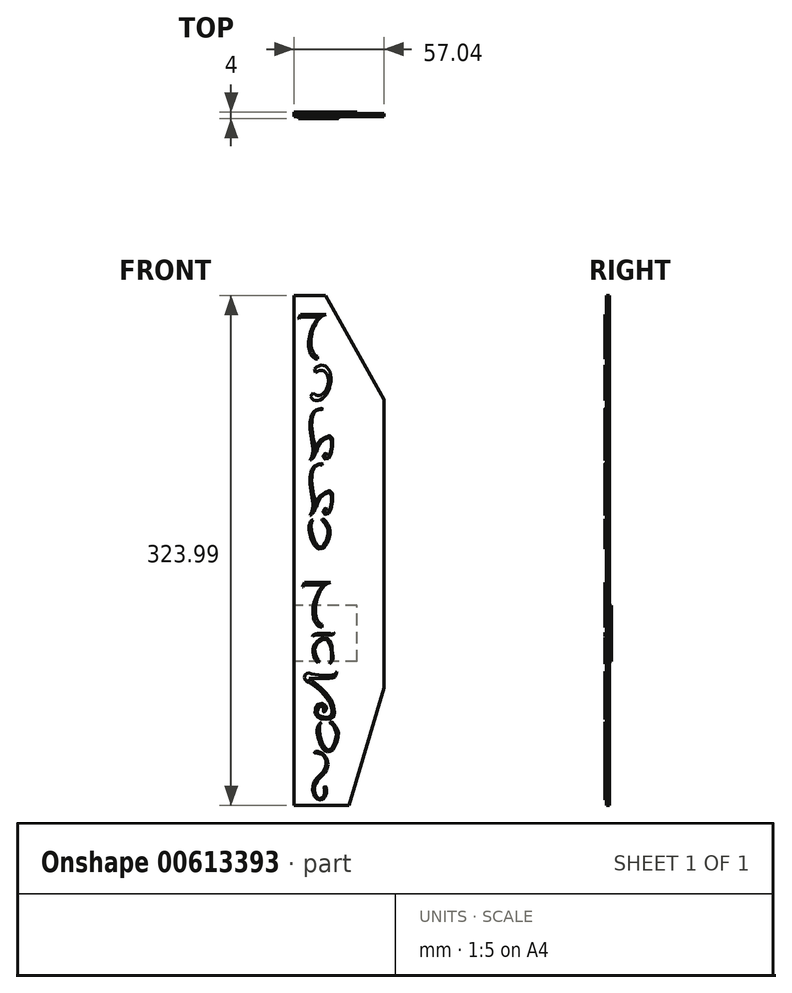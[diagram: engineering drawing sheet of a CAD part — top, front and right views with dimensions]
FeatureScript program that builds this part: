
annotation { "Feature Type Name" : "Feature", "Feature Type Description" : "" }
export const myFeature = defineFeature(function(context is Context, id is Id, definition is map)
    precondition{}
    {
        {
            var Q0;
            Q0=qCreatedBy(makeId("Front.planeOp"),FACE);
            var sketch = newSketch(context, id + "F0", { "sketchPlane" : qUnion([Q0])});
            skLineSegment(sketch, "E0", {"start": v(0, 0) * mm, "end": v(40, 0) * mm});
            skLineSegment(sketch, "E1", {"start": v(40, 0) * mm, "end": v(57.04, 0) * mm});
            skLineSegment(sketch, "E2", {"start": v(57.04, 0) * mm, "end": v(57.04, 166.67) * mm});
            skLineSegment(sketch, "E3", {"start": v(0, 200) * mm, "end": v(0, 0) * mm});
            skLineSegment(sketch, "E4", {"start": v(57.04, 166.67) * mm, "end": v(19.79, 232.6) * mm});
            skPoint(sketch, "E5.center.orphan", {"position": v(28.52, 183.33) * mm});
            skLineSegment(sketch, "E6", {"start": v(19.79, 232.6) * mm, "end": v(0, 232.6) * mm});
            skLineSegment(sketch, "E7", {"start": v(0, 232.6) * mm, "end": v(0, 200) * mm});
            skLineSegment(sketch, "E8", {"start": v(57.04, 0) * mm, "end": v(57.04, -16.7) * mm});
            skLineSegment(sketch, "E9", {"start": v(34.85, -91.4) * mm, "end": v(0, -91.4) * mm});
            skLineSegment(sketch, "E10", {"start": v(0, -91.4) * mm, "end": v(0, 0) * mm});
            skLineSegment(sketch, "E11", {"start": v(34.85, -91.4) * mm, "end": v(57.04, -16.7) * mm});
            skSolve(sketch);
        }
        {
            var Q0;
            Q0=makeQuery(id+"F0.imprint","IMPRINT",FACE,{"disambiguationData":[TD([[makeQuery(id+"F0.imprint","IMPRINT",EDGE,{"derivedFrom":sQuery(id+"F0.wireOp",EDGE,"E0")}),1.0]])]});
            var Q1;
            Q1=makeQuery(id+"F0.imprint","IMPRINT",FACE,{"disambiguationData":[TD([[makeQuery(id+"F0.imprint","IMPRINT",EDGE,{"derivedFrom":sQuery(id+"F0.wireOp",EDGE,"E0")}),-1.0]])]});
            extrude(context, id + "F1", {"entities" : qUnion([Q0, Q1]), "depth" : 2 * mm, "offsetDistance" : 25 * mm});
        }
        {
            var Q0;
            Q0=makeQuery(id+"F1.opExtrude","CAP_FACE",FACE,{"disambiguationData":[OSD([sQuery(id+"F0.wireOp",EDGE,"E0"),sQuery(id+"F0.wireOp",EDGE,"E1"),sQuery(id+"F0.wireOp",EDGE,"E2"),sQuery(id+"F0.wireOp",EDGE,"E3"),sQuery(id+"F0.wireOp",EDGE,"E4"),sQuery(id+"F0.wireOp",EDGE,"E6"),sQuery(id+"F0.wireOp",EDGE,"E7")])],"isStart":true});
            var sketch = newSketch(context, id + "F2", { "sketchPlane" : qUnion([Q0])});
            skLineSegment(sketch, "E12.bottom", {"start": v(-40, 0) * mm, "end": v(0, 0) * mm});
            skLineSegment(sketch, "E12.top", {"start": v(-40, 35.71) * mm, "end": v(0, 35.71) * mm});
            skLineSegment(sketch, "E12.left", {"start": v(-40, 0) * mm, "end": v(-40, 35.71) * mm});
            skLineSegment(sketch, "E12.right", {"start": v(0, 0) * mm, "end": v(0, 35.71) * mm});
            skSolve(sketch);
        }
        {
            var Q0;
            Q0=makeQuery(id+"F2.imprint","IMPRINT",FACE,{"disambiguationData":[TD([[makeQuery(id+"F2.imprint","IMPRINT",EDGE,{"derivedFrom":sQuery(id+"F2.wireOp",EDGE,"E12.bottom")}),1.0]])]});
            extrude(context, id + "F3", {"entities" : qUnion([Q0]), "operationType" : NewBodyOperationType.ADD, "depth" : 1 * mm, "offsetDistance" : 25 * mm});
        }
        {
            var Q0;
            Q0=makeQuery(id+"F1.opExtrude","CAP_FACE",FACE,{"disambiguationData":[OSD([sQuery(id+"F0.wireOp",EDGE,"E2"),sQuery(id+"F0.wireOp",EDGE,"E3"),sQuery(id+"F0.wireOp",EDGE,"E4"),sQuery(id+"F0.wireOp",EDGE,"E6"),sQuery(id+"F0.wireOp",EDGE,"E7"),sQuery(id+"F0.wireOp",EDGE,"E8"),sQuery(id+"F0.wireOp",EDGE,"E9"),sQuery(id+"F0.wireOp",EDGE,"E10"),sQuery(id+"F0.wireOp",EDGE,"E11")])],"isStart":false});
            var sketch = newSketch(context, id + "F4", { "sketchPlane" : qUnion([Q0])});
            skSolve(sketch);
        }
        {
            var Q0;
            Q0=makeQuery(id+"F4.imprint","IMPRINT",FACE,{"disambiguationData":[TD([[makeQuery(id+"F4.imprint","IMPRINT",EDGE,{"derivedFrom":makeQuery(id+"F1.opExtrude","CAP_EDGE",EDGE,{"disambiguationData":[OSD([sQuery(id+"F0.wireOp",EDGE,"E4")])],"isStart":false})}),1.0]])]});
            var sketch = newSketch(context, id + "F5", { "sketchPlane" : qUnion([Q0])});
            skLineSegment(sketch, "E13", {"start": v(3.86, 220.53) * mm, "end": v(7.1, 220.53) * mm});
            skLineSegment(sketch, "E14", {"start": v(3.86, 220.53) * mm, "end": v(2.57, 217.83) * mm});
            skLineSegment(sketch, "E15", {"start": v(2.57, 217.83) * mm, "end": v(2.95, 217.65) * mm});
            skLineSegment(sketch, "E16", {"start": v(2.95, 217.65) * mm, "end": v(3.53, 218.87) * mm});
            skLineSegment(sketch, "E17", {"start": v(3.53, 218.87) * mm, "end": v(15.74, 218.87) * mm});
            skEllipticalArc(sketch, "E18", {});
            skEllipticalArc(sketch, "E19", {});
            skLineSegment(sketch, "E20", {"start": v(7.1, 220.53) * mm, "end": v(20.2, 220.53) * mm});
            skLineSegment(sketch, "E21", {"start": v(14.85, 192.12) * mm, "end": v(14.85, 193.83) * mm});
            skEllipticalArc(sketch, "E22", {});
            skEllipticalArc(sketch, "E23", {});
            skLineSegment(sketch, "E24", {"start": v(13.62, 183.6) * mm, "end": v(12.94, 185.8) * mm});
            skLineSegment(sketch, "E25", {"start": v(11.98, 170.7) * mm, "end": v(10.28, 168.38) * mm});
            skFitSpline(sketch, "E26", {"points": [v(16.98, 160.68) * mm, v(13.52, 159.57) * mm, v(11.18, 157.11) * mm, v(10.06, 148.08) * mm, v(11.85, 134.58) * mm, v(10.17, 127.77) * mm], "startDerivative": vector(-25.24, -6.07) * mm, "endDerivative": vector(-12.16, -30.27) * mm});
            skFitSpline(sketch, "E27", {"points": [v(10.17, 127.77) * mm, v(12.3, 129.8) * mm, v(13.3, 132.12) * mm, v(15.2, 139.15) * mm, v(19.55, 142.39) * mm, v(23.45, 143.4) * mm, v(23.67, 133.13) * mm, v(21, 128.66) * mm, v(18.68, 129.12) * mm, v(18.74, 131.71) * mm, v(20.8, 132.38) * mm, v(20.4, 131.51) * mm, v(19.54, 131.25) * mm, v(19.87, 129.2) * mm, v(21.23, 129.27) * mm, v(23.12, 133.02) * mm, v(23.12, 141.9) * mm, v(20.5, 141.9) * mm, v(16.18, 138.62) * mm, v(14.14, 133.1) * mm], "startDerivative": vector(50.8, 43.85) * mm, "endDerivative": vector(-20, -100.63) * mm});
            skFitSpline(sketch, "E28", {"points": [v(14.14, 133.1) * mm, v(13.3, 132.12) * mm], "startDerivative": vector(-0.84, -0.98) * mm, "endDerivative": vector(-0.84, -0.98) * mm});
            skFitSpline(sketch, "E29", {"points": [v(16.98, 160.68) * mm, v(17.97, 160.68) * mm, v(17.57, 160.04) * mm, v(16.7, 160.14) * mm, v(13.9, 159.27) * mm, v(12.1, 157.11) * mm, v(11.18, 148.08) * mm, v(13.3, 136.6) * mm, v(13.66, 134.03) * mm], "startDerivative": vector(19.65, 3.96) * mm, "endDerivative": vector(1.63, -18.4) * mm});
            skFitSpline(sketch, "E30", {"points": [v(16.98, 125.68) * mm, v(13.52, 124.57) * mm, v(11.18, 122.11) * mm, v(10.06, 113.08) * mm, v(11.85, 99.58) * mm, v(10.17, 92.77) * mm], "startDerivative": vector(-25.24, -6.07) * mm, "endDerivative": vector(-12.16, -30.27) * mm});
            skFitSpline(sketch, "E31", {"points": [v(10.17, 92.77) * mm, v(12.3, 94.8) * mm, v(13.3, 97.12) * mm, v(15.2, 104.15) * mm, v(19.55, 107.39) * mm, v(23.45, 108.4) * mm, v(23.67, 98.13) * mm, v(21, 93.66) * mm, v(18.68, 94.12) * mm, v(18.74, 96.71) * mm, v(20.8, 97.38) * mm, v(20.4, 96.51) * mm, v(19.54, 96.25) * mm, v(19.87, 94.2) * mm, v(21.23, 94.27) * mm, v(23.12, 98.02) * mm, v(23.12, 106.9) * mm, v(20.5, 106.9) * mm, v(16.18, 103.62) * mm, v(14.14, 98.1) * mm], "startDerivative": vector(50.8, 43.85) * mm, "endDerivative": vector(-20, -100.63) * mm});
            skFitSpline(sketch, "E32", {"points": [v(14.14, 98.1) * mm, v(13.3, 97.12) * mm], "startDerivative": vector(-0.84, -0.98) * mm, "endDerivative": vector(-0.84, -0.98) * mm});
            skFitSpline(sketch, "E33", {"points": [v(16.98, 125.68) * mm, v(17.97, 125.68) * mm, v(17.57, 125.04) * mm, v(16.7, 125.14) * mm, v(13.9, 124.27) * mm, v(12.1, 122.11) * mm, v(11.18, 113.08) * mm, v(13.3, 101.6) * mm, v(13.66, 99.03) * mm], "startDerivative": vector(19.65, 3.96) * mm, "endDerivative": vector(1.63, -18.4) * mm});
            skFitSpline(sketch, "E34", {"points": [v(12.01, 90.1) * mm, v(10.84, 87.57) * mm, v(12.7, 77.09) * mm, v(16.05, 72.72) * mm], "startDerivative": vector(-6.54, -8.17) * mm, "endDerivative": vector(11.14, -10.32) * mm});
            skFitSpline(sketch, "E35", {"points": [v(12.01, 90.1) * mm, v(10.84, 89.48) * mm, v(9.9, 87.57) * mm, v(9.38, 84.05) * mm, v(12.7, 73.94) * mm, v(15.88, 71.56) * mm], "startDerivative": vector(-10.77, -3.6) * mm, "endDerivative": vector(15.89, -6.97) * mm});
            skFitSpline(sketch, "E36", {"points": [v(16.05, 72.72) * mm, v(18.2, 73.3) * mm, v(19.78, 75.83) * mm, v(21.47, 81.19) * mm, v(20.86, 85.67) * mm, v(19.09, 88.5) * mm, v(17.5, 90.1) * mm, v(18.25, 90.66) * mm, v(19.73, 89.48) * mm, v(22.25, 85.7) * mm, v(22.7, 80.87) * mm, v(19.15, 72.72) * mm, v(15.88, 71.56) * mm], "startDerivative": vector(35.6, 3.82) * mm, "endDerivative": vector(-40.74, -3.34) * mm});
            skLineSegment(sketch, "E37", {"start": v(6.62, 50.23) * mm, "end": v(9.84, 50.23) * mm});
            skLineSegment(sketch, "E38", {"start": v(6.62, 50.23) * mm, "end": v(5.32, 47.54) * mm});
            skLineSegment(sketch, "E39", {"start": v(5.32, 47.54) * mm, "end": v(5.7, 47.36) * mm});
            skLineSegment(sketch, "E40", {"start": v(5.7, 47.36) * mm, "end": v(6.29, 48.57) * mm});
            skLineSegment(sketch, "E41", {"start": v(6.29, 48.57) * mm, "end": v(18.5, 48.57) * mm});
            skEllipticalArc(sketch, "E42", {});
            skEllipticalArc(sketch, "E43", {});
            skLineSegment(sketch, "E44", {"start": v(9.84, 50.23) * mm, "end": v(22.95, 50.23) * mm});
            skLineSegment(sketch, "E45", {"start": v(17.6, 21.82) * mm, "end": v(17.6, 23.54) * mm});
            skFitSpline(sketch, "E46", {"points": [v(15, -0.86) * mm, v(13.02, 2.13) * mm, v(11.87, 6.75) * mm, v(13.24, 11.32) * mm, v(18.87, 15.3) * mm, v(23.06, 12.43) * mm, v(24.3, 5.5) * mm, v(24.36, 1.07) * mm, v(22.4, -1.35) * mm], "startDerivative": vector(-19.8, 25.5) * mm, "endDerivative": vector(-24.34, -21.8) * mm});
            skFitSpline(sketch, "E47", {"points": [v(15, -0.86) * mm, v(15.51, 0.65) * mm, v(14.29, 2.7) * mm, v(13.02, 6.63) * mm, v(14.29, 11) * mm, v(18.86, 14.22) * mm, v(22.16, 11.89) * mm, v(23.62, 5.59) * mm, v(23.68, 1.3) * mm, v(22.4, -1.35) * mm], "startDerivative": vector(12.33, 21.15) * mm, "endDerivative": vector(-16.23, -25.62) * mm});
            skFitSpline(sketch, "E48", {"points": [v(11.67, 16.35) * mm, v(12.3, 17.03) * mm, v(13.71, 17.64) * mm, v(22.93, 17.91) * mm], "startDerivative": vector(3.18, 3.9) * mm, "endDerivative": vector(19.32, -0.2) * mm});
            skFitSpline(sketch, "E49", {"points": [v(22.93, 17.91) * mm, v(23.8, 17.37) * mm, v(24.93, 17.91) * mm, v(25, 18.57) * mm], "startDerivative": vector(2.24, -2.27) * mm, "endDerivative": vector(-0.34, 2.4) * mm});
            skFitSpline(sketch, "E50", {"points": [v(25, 18.57) * mm, v(25.26, 18.3) * mm, v(25.18, 17.84) * mm, v(24.53, 17.21) * mm, v(23.5, 16.97) * mm, v(22.4, 17.06) * mm, v(13.57, 16.88) * mm, v(12.8, 16.6) * mm, v(12.33, 16.41) * mm, v(11.59, 15.96) * mm], "startDerivative": vector(5.2, -3.62) * mm, "endDerivative": vector(-8.06, -5.5) * mm});
            skFitSpline(sketch, "E51", {"points": [v(11.67, 16.35) * mm, v(11.59, 15.96) * mm], "startDerivative": vector(-0.08, -0.4) * mm, "endDerivative": vector(-0.08, -0.4) * mm});
            skFitSpline(sketch, "E52", {"points": [v(27.09, -6.15) * mm, v(25.65, -7.96) * mm, v(22, -8.61) * mm, v(12.36, -8.02) * mm, v(7.91, -7.46) * mm, v(6.49, -10.7) * mm, v(9.7, -13.3) * mm, v(15.49, -17.53) * mm, v(20.5, -22.94) * mm], "startDerivative": vector(-13.85, -20.96) * mm, "endDerivative": vector(50.43, -64.75) * mm});
            skFitSpline(sketch, "E53", {"points": [v(20.5, -22.94) * mm, v(23.39, -28.15) * mm, v(23.23, -34.3) * mm, v(18.02, -35.1) * mm, v(14.7, -31.15) * mm], "startDerivative": vector(11.95, -17.68) * mm, "endDerivative": vector(8.08, 21.68) * mm});
            skFitSpline(sketch, "E54", {"points": [v(14.7, -31.15) * mm, v(16.29, -28.46) * mm, v(18.97, -29.25) * mm, v(18.31, -31.15) * mm, v(19.06, -32.21) * mm, v(19.81, -31.15) * mm, v(20.56, -29.02) * mm, v(18.87, -26.96) * mm, v(15.4, -26.77) * mm, v(13.15, -31.15) * mm, v(14.7, -35.12) * mm, v(18.02, -36.53) * mm, v(23.1, -36.43) * mm, v(24.88, -35.1) * mm, v(24.97, -28.08) * mm, v(19.25, -18.89) * mm, v(9.4, -10.54) * mm], "startDerivative": vector(15.98, 63.28) * mm, "endDerivative": vector(-91.6, 70.25) * mm});
            skFitSpline(sketch, "E55", {"points": [v(9.4, -10.54) * mm, v(21.97, -10.54) * mm, v(25.82, -9.5) * mm, v(27.09, -6.15) * mm], "startDerivative": vector(29.6, -0.49) * mm, "endDerivative": vector(3.16, 15.37) * mm});
            skFitSpline(sketch, "E56", {"points": [v(17.21, -38.69) * mm, v(16.04, -41.22) * mm, v(17.9, -51.7) * mm, v(21.25, -56.07) * mm], "startDerivative": vector(-6.54, -8.17) * mm, "endDerivative": vector(11.14, -10.32) * mm});
            skFitSpline(sketch, "E57", {"points": [v(17.21, -38.69) * mm, v(16.04, -39.31) * mm, v(15.1, -41.22) * mm, v(14.58, -44.74) * mm, v(17.9, -54.85) * mm, v(21.08, -57.24) * mm], "startDerivative": vector(-10.77, -3.6) * mm, "endDerivative": vector(15.89, -6.97) * mm});
            skFitSpline(sketch, "E58", {"points": [v(21.25, -56.07) * mm, v(23.4, -55.49) * mm, v(24.98, -52.96) * mm, v(26.67, -47.6) * mm, v(26.06, -43.12) * mm, v(24.29, -40.3) * mm, v(22.7, -38.69) * mm, v(23.45, -38.13) * mm, v(24.93, -39.31) * mm, v(27.45, -43.1) * mm, v(27.9, -47.92) * mm, v(24.35, -56.07) * mm, v(21.08, -57.24) * mm], "startDerivative": vector(35.6, 3.82) * mm, "endDerivative": vector(-40.74, -3.34) * mm});
            skFitSpline(sketch, "E59", {"points": [v(13.66, -56.9) * mm, v(17.04, -57.74) * mm, v(19.76, -60.09) * mm, v(21.17, -63.28) * mm, v(21.08, -66.94) * mm, v(18.82, -71.35) * mm, v(15.54, -74.82) * mm, v(13.66, -77.82) * mm, v(12.82, -81.95) * mm, v(13.94, -84.86) * mm, v(15.92, -87.02) * mm], "startDerivative": vector(36.83, -5.4) * mm, "endDerivative": vector(51.01, -25.5) * mm});
            skFitSpline(sketch, "E60", {"points": [v(15.92, -87.02) * mm, v(18.07, -86.17) * mm, v(19.1, -83.92) * mm, v(19.2, -80.73) * mm, v(18.45, -80.07) * mm], "startDerivative": vector(9.38, 2.2) * mm, "endDerivative": vector(-5.22, 2.52) * mm});
            skFitSpline(sketch, "E61", {"points": [v(18.45, -80.07) * mm, v(19.5, -79.32) * mm, v(20.37, -80.21) * mm, v(20.21, -84.3) * mm, v(18.74, -87.02) * mm, v(16.9, -87.92) * mm, v(13.98, -87.02) * mm, v(12.4, -84.3) * mm, v(11.7, -81.95) * mm, v(12, -77.98) * mm, v(14.14, -74.35) * mm, v(17.61, -70.8) * mm, v(20.06, -66.86) * mm, v(20.14, -63.15) * mm, v(18.74, -60.07) * mm, v(15.92, -58.34) * mm, v(12.8, -57.86) * mm, v(13.66, -56.9) * mm], "startDerivative": vector(27, 28.36) * mm, "endDerivative": vector(-10.77, 30.94) * mm});
            skLineSegment(sketch, "E62", {"start": v(0, -76.84) * mm, "end": v(0, -91.4) * mm});
            skLineSegment(sketch, "E63", {"start": v(0, -91.4) * mm, "end": v(8.12, -91.4) * mm});
            const initialGuessF5  = {"E18": [0.018544869471057976, 0.20709701367466082, 0.3140856699790382, 0.9493946449784825, 0.015537334011104582, 0.008485907113070932, 0.6388991419615133, 3.2831460951122216], "E19": [0.018544869471057976, 0.20709701367466082, 0.24253552143487014, 0.9701425260456917, 0.013780557752704876, 0.007388543269675694, 0.2259031223263688, 3.0918384497159117], "E22": [0.0160642727871564, 0.17704404071716898, 0.2313512452415796, 0.9728702900824809, 0.011468486584754524, 0.006902209779284208, 2.589616745986262, 0.8233252755202504], "E23": [0.0160642727871564, 0.17704404071716898, 0.21490751269293634, 0.9766344049787186, 0.008016117309888379, 0.005600430553553324, 2.654079908501021, 0.746419326042122], "E42": [0.021298223862533633, 0.03680388277507052, 0.3140856699790382, 0.9493946449784825, 0.015537334011104582, 0.008485907113070932, 0.6388991419615132, 3.28314609511222], "E43": [0.021298223862533633, 0.03680388277507052, 0.24253552143487014, 0.9701425260456917, 0.013780557752704876, 0.007388543269675694, 0.22590312232636875, 3.0918384497159126]};
            skSetInitialGuess(sketch, initialGuessF5);
            skSolve(sketch);
        }
        {
            var Q0;
            Q0 = qSketchRegion(id + "F5", true);
            extrude(context, id + "F6", {"entities" : qUnion([Q0]), "operationType" : NewBodyOperationType.ADD, "depth" : 1 * mm, "offsetDistance" : 25 * mm});
        }
    });
